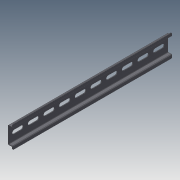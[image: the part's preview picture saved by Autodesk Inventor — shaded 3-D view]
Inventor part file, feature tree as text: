
AUTODESK INVENTOR PART (.ipt)
format: ipt  version: 2020.3 (Build 243373000, 373)  size: 237,568 bytes
history: native  units: in
note: dims shown in document units (in); Inventor stores cm internally (conversion verified against a paired STEP export)
features: extrude x1, fillet x1, sketch x1, other x1
ambient origin geometry x8: Origin, YZ Plane, XZ Plane, XY Plane, X Axis, Y Axis, Z Axis, Center Point
bodies: Solid1 (feature_tree)
feature tree (4):
  extrude  "Extrusion1"  Depth=0.0625in TaperAngle=0.0deg
  fillet  "Fillet1"  Radius=0.0625in
  sketch  "Sketch1"  dims[d0=10.0in d1=1.0in d2=0.0in d3=0.0625in]
  other  "LPattern1"
